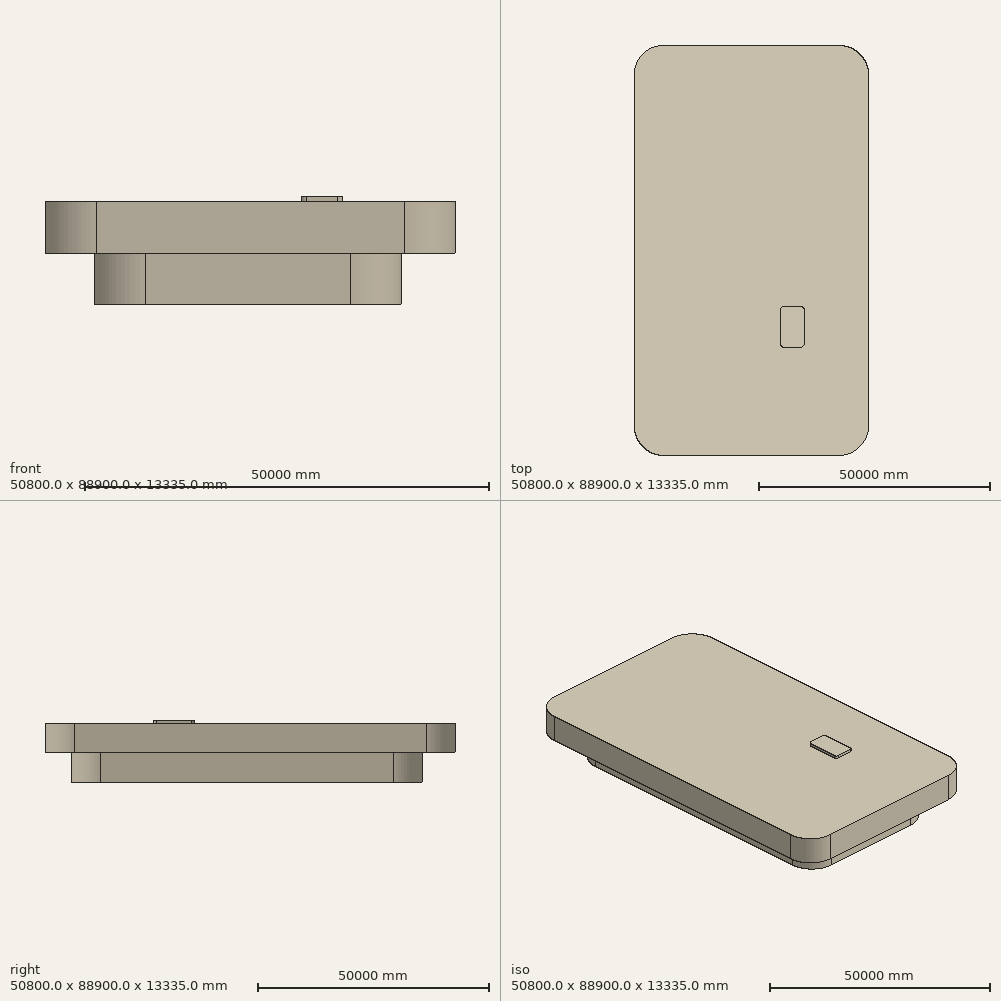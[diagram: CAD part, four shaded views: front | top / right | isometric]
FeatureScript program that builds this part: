
annotation { "Feature Type Name" : "Feature", "Feature Type Description" : "" }
export const myFeature = defineFeature(function(context is Context, id is Id, definition is map)
    precondition{}
    {
        {
            var Q0;
            Q0=qCreatedBy(makeId("Top.planeOp"),FACE);
            var sketch = newSketch(context, id + "F0", { "sketchPlane" : qUnion([Q0])});
            skLineSegment(sketch, "E0.bottom", {"start": v(591.8, -694.37) * mm, "end": v(1353.8, -694.37) * mm});
            skLineSegment(sketch, "E0.top", {"start": v(591.8, -186.37) * mm, "end": v(1353.8, -186.37) * mm});
            skLineSegment(sketch, "E0.left", {"start": v(528.3, -630.87) * mm, "end": v(528.3, -249.87) * mm});
            skLineSegment(sketch, "E0.right", {"start": v(1417.3, -630.87) * mm, "end": v(1417.3, -249.87) * mm});
            skPoint(sketch, "E1.visualSharp", {"position": v(1417.3, -186.37) * mm});
            skArc(sketch, "E1.filletArc", {"start": v(1417.3, -249.87) * mm, "mid": v(1398.7, -204.97) * mm, "end": v(1353.8, -186.37) * mm});
            skPoint(sketch, "E2.visualSharp", {"position": v(1417.3, -694.37) * mm});
            skArc(sketch, "E2.filletArc", {"start": v(1353.8, -694.37) * mm, "mid": v(1398.7, -675.78) * mm, "end": v(1417.3, -630.87) * mm});
            skPoint(sketch, "E3.visualSharp", {"position": v(528.3, -694.37) * mm});
            skArc(sketch, "E3.filletArc", {"start": v(528.3, -630.87) * mm, "mid": v(546.9, -675.78) * mm, "end": v(591.8, -694.37) * mm});
            skPoint(sketch, "E4.visualSharp", {"position": v(528.3, -186.37) * mm});
            skArc(sketch, "E4.filletArc", {"start": v(591.8, -186.37) * mm, "mid": v(546.9, -204.97) * mm, "end": v(528.3, -249.87) * mm});
            skSolve(sketch);
        }
        {
            var Q0;
            Q0 = qSketchRegion(id + "F0", true);
            extrude(context, id + "F1", {"entities" : qUnion([Q0]), "depth" : 6.35 * mm});
        }
        {
            var Q0;
            Q0=makeQuery(id+"F1.opExtrude","CAP_FACE",FACE,{"disambiguationData":[OSD([sQuery(id+"F0.wireOp",EDGE,"E0.bottom"),sQuery(id+"F0.wireOp",EDGE,"E0.top"),sQuery(id+"F0.wireOp",EDGE,"E0.left"),sQuery(id+"F0.wireOp",EDGE,"E0.right"),sQuery(id+"F0.wireOp",EDGE,"E1.filletArc"),sQuery(id+"F0.wireOp",EDGE,"E2.filletArc"),sQuery(id+"F0.wireOp",EDGE,"E3.filletArc"),sQuery(id+"F0.wireOp",EDGE,"E4.filletArc")])],"isStart":false});
            cPlane(context, id + "F2", {"entities" : qUnion([Q0]), "cplaneType" : CPlaneType.OFFSET, "offset" : 25.4 * mm, "width" : 152.4 * mm, "height" : 152.4 * mm});
        }
        {
            var Q0;
            Q0=qCreatedBy(id+"F2.planeOp",FACE);
            var sketch = newSketch(context, id + "F3", { "sketchPlane" : qUnion([Q0])});
            skLineSegment(sketch, "E5.bottom", {"start": v(591.8, -694.37) * mm, "end": v(1353.8, -694.37) * mm});
            skLineSegment(sketch, "E5.top", {"start": v(591.8, -186.37) * mm, "end": v(1353.8, -186.37) * mm});
            skLineSegment(sketch, "E5.left", {"start": v(528.3, -630.87) * mm, "end": v(528.3, -249.87) * mm});
            skLineSegment(sketch, "E5.right", {"start": v(1417.3, -630.87) * mm, "end": v(1417.3, -249.87) * mm});
            skPoint(sketch, "E6.visualSharp", {"position": v(1417.3, -186.37) * mm});
            skArc(sketch, "E6.filletArc", {"start": v(1417.3, -249.87) * mm, "mid": v(1398.7, -204.97) * mm, "end": v(1353.8, -186.37) * mm});
            skPoint(sketch, "E7.visualSharp", {"position": v(1417.3, -694.37) * mm});
            skArc(sketch, "E7.filletArc", {"start": v(1353.8, -694.37) * mm, "mid": v(1398.7, -675.78) * mm, "end": v(1417.3, -630.87) * mm});
            skPoint(sketch, "E8.visualSharp", {"position": v(528.3, -694.37) * mm});
            skArc(sketch, "E8.filletArc", {"start": v(528.3, -630.87) * mm, "mid": v(546.9, -675.78) * mm, "end": v(591.8, -694.37) * mm});
            skPoint(sketch, "E9.visualSharp", {"position": v(528.3, -186.37) * mm});
            skArc(sketch, "E9.filletArc", {"start": v(591.8, -186.37) * mm, "mid": v(546.9, -204.97) * mm, "end": v(528.3, -249.87) * mm});
            skSolve(sketch);
        }
        {
            var Q0;
            Q0=makeQuery(id+"F3.imprint","IMPRINT",FACE,{"disambiguationData":[TD([[makeQuery(id+"F3.imprint","IMPRINT",EDGE,{"derivedFrom":sQuery(id+"F3.wireOp",EDGE,"E5.bottom")}),1.0]])]});
            var Q1;
            Q1=sQuery(id+"F3.wireOp",EDGE,"E5.right");
            var Q2;
            Q2=sQuery(id+"F3.wireOp",EDGE,"E8.filletArc");
            var Q3;
            Q3=sQuery(id+"F3.wireOp",EDGE,"E6.filletArc");
            var Q4;
            Q4=sQuery(id+"F3.wireOp",EDGE,"E5.bottom");
            var Q5;
            Q5=sQuery(id+"F3.wireOp",EDGE,"E9.filletArc");
            var Q6;
            Q6=sQuery(id+"F3.wireOp",EDGE,"E7.filletArc");
            var Q7;
            Q7=sQuery(id+"F3.wireOp",EDGE,"E5.top");
            var Q8;
            Q8=sQuery(id+"F3.wireOp",EDGE,"E5.left");
            extrude(context, id + "F4", {"entities" : qUnion([Q0]), "surfaceEntities" : qUnion([Q1, Q2, Q3, Q4, Q5, Q6, Q7, Q8]), "depth" : 6.35 * mm});
        }
        {
            var Q0;
            Q0=qCreatedBy(id+"F2.planeOp",FACE);
            cPlane(context, id + "F5", {"entities" : qUnion([Q0]), "cplaneType" : CPlaneType.OFFSET, "offset" : 25.4 * mm, "width" : 152.4 * mm, "height" : 152.4 * mm});
        }
        {
            var Q0;
            Q0=qCreatedBy(id+"F5.planeOp",FACE);
            var sketch = newSketch(context, id + "F6", { "sketchPlane" : qUnion([Q0])});
            skLineSegment(sketch, "E10.bottom", {"start": v(591.8, -694.37) * mm, "end": v(1353.8, -694.37) * mm});
            skLineSegment(sketch, "E10.top", {"start": v(591.8, -186.37) * mm, "end": v(1353.8, -186.37) * mm});
            skLineSegment(sketch, "E10.left", {"start": v(528.3, -630.87) * mm, "end": v(528.3, -249.87) * mm});
            skLineSegment(sketch, "E10.right", {"start": v(1417.3, -630.87) * mm, "end": v(1417.3, -249.87) * mm});
            skPoint(sketch, "E11.visualSharp", {"position": v(1417.3, -186.37) * mm});
            skArc(sketch, "E11.filletArc", {"start": v(1417.3, -249.87) * mm, "mid": v(1398.7, -204.97) * mm, "end": v(1353.8, -186.37) * mm});
            skPoint(sketch, "E12.visualSharp", {"position": v(1417.3, -694.37) * mm});
            skArc(sketch, "E12.filletArc", {"start": v(1353.8, -694.37) * mm, "mid": v(1398.7, -675.78) * mm, "end": v(1417.3, -630.87) * mm});
            skPoint(sketch, "E13.visualSharp", {"position": v(528.3, -694.37) * mm});
            skArc(sketch, "E13.filletArc", {"start": v(528.3, -630.87) * mm, "mid": v(546.9, -675.78) * mm, "end": v(591.8, -694.37) * mm});
            skPoint(sketch, "E14.visualSharp", {"position": v(528.3, -186.37) * mm});
            skArc(sketch, "E14.filletArc", {"start": v(591.8, -186.37) * mm, "mid": v(546.9, -204.97) * mm, "end": v(528.3, -249.87) * mm});
            skSolve(sketch);
        }
        {
            var Q0;
            Q0 = qSketchRegion(id + "F6", true);
            var Q1;
            Q1=makeQuery(id+"F6.imprint","IMPRINT",FACE,{"disambiguationData":[TD([[makeQuery(id+"F6.imprint","IMPRINT",EDGE,{"derivedFrom":sQuery(id+"F6.wireOp",EDGE,"E10.bottom")}),1.0]])]});
            extrude(context, id + "F7", {"entities" : qUnion([Q0, Q1]), "depth" : 6.35 * mm});
        }
        {
            var Q0;
            Q0=qCreatedBy(makeId("Top.planeOp"),FACE);
            var sketch = newSketch(context, id + "F8", { "sketchPlane" : qUnion([Q0])});
            skLineSegment(sketch, "E15.bottom", {"start": v(-2759.22, -3519.53) * mm, "end": v(1050.78, -3519.53) * mm});
            skLineSegment(sketch, "E15.top", {"start": v(-2759.22, 5370.47) * mm, "end": v(1050.78, 5370.47) * mm});
            skLineSegment(sketch, "E15.left", {"start": v(-3394.22, -2884.53) * mm, "end": v(-3394.22, 4735.47) * mm});
            skLineSegment(sketch, "E15.right", {"start": v(1685.78, -2884.53) * mm, "end": v(1685.78, 4735.47) * mm});
            skPoint(sketch, "E16.visualSharp", {"position": v(1685.78, 5370.47) * mm});
            skArc(sketch, "E16.filletArc", {"start": v(1685.78, 4735.47) * mm, "mid": v(1499.8, 5184.48) * mm, "end": v(1050.78, 5370.47) * mm});
            skPoint(sketch, "E17.visualSharp", {"position": v(-3394.22, 5370.47) * mm});
            skArc(sketch, "E17.filletArc", {"start": v(-2759.22, 5370.47) * mm, "mid": v(-3208.23, 5184.48) * mm, "end": v(-3394.22, 4735.47) * mm});
            skPoint(sketch, "E18.visualSharp", {"position": v(-3394.22, -3519.53) * mm});
            skArc(sketch, "E18.filletArc", {"start": v(-3394.22, -2884.53) * mm, "mid": v(-3208.23, -3333.54) * mm, "end": v(-2759.22, -3519.53) * mm});
            skPoint(sketch, "E19.visualSharp", {"position": v(1685.78, -3519.53) * mm});
            skArc(sketch, "E19.filletArc", {"start": v(1050.78, -3519.53) * mm, "mid": v(1499.8, -3333.54) * mm, "end": v(1685.78, -2884.53) * mm});
            skSolve(sketch);
        }
        {
            var Q0;
            Q0=makeQuery(id+"F8.imprint","IMPRINT",FACE,{"disambiguationData":[TD([[makeQuery(id+"F8.imprint","IMPRINT",EDGE,{"derivedFrom":sQuery(id+"F8.wireOp",EDGE,"E15.bottom")}),1.0]])]});
            extrude(context, id + "F9", {"entities" : qUnion([Q0]), "depth" : 635 * mm});
        }
        {
            var Q0;
            Q0=makeQuery(id+"F9.opExtrude","CAP_FACE",FACE,{"disambiguationData":[OSD([sQuery(id+"F8.wireOp",EDGE,"E15.bottom"),sQuery(id+"F8.wireOp",EDGE,"E15.top"),sQuery(id+"F8.wireOp",EDGE,"E15.left"),sQuery(id+"F8.wireOp",EDGE,"E15.right"),sQuery(id+"F8.wireOp",EDGE,"E16.filletArc"),sQuery(id+"F8.wireOp",EDGE,"E17.filletArc"),sQuery(id+"F8.wireOp",EDGE,"E18.filletArc"),sQuery(id+"F8.wireOp",EDGE,"E19.filletArc")])],"isStart":true});
            var sketch = newSketch(context, id + "F10", { "sketchPlane" : qUnion([Q0])});
            skLineSegment(sketch, "E20.bottom", {"start": v(-28802.53, 26934.52) * mm, "end": v(9297.47, 26934.52) * mm});
            skLineSegment(sketch, "E20.top", {"start": v(-28802.53, -61965.48) * mm, "end": v(9297.47, -61965.48) * mm});
            skLineSegment(sketch, "E20.left", {"start": v(-35152.53, 20584.52) * mm, "end": v(-35152.53, -55615.48) * mm});
            skLineSegment(sketch, "E20.right", {"start": v(15647.47, 20584.52) * mm, "end": v(15647.47, -55615.48) * mm});
            skPoint(sketch, "E21.visualSharp", {"position": v(15647.47, -61965.48) * mm});
            skArc(sketch, "E21.filletArc", {"start": v(9297.47, -61965.48) * mm, "mid": v(13787.6, -60105.6) * mm, "end": v(15647.47, -55615.48) * mm});
            skPoint(sketch, "E22.visualSharp", {"position": v(-35152.53, -61965.48) * mm});
            skArc(sketch, "E22.filletArc", {"start": v(-35152.53, -55615.48) * mm, "mid": v(-33292.66, -60105.6) * mm, "end": v(-28802.53, -61965.48) * mm});
            skPoint(sketch, "E23.visualSharp", {"position": v(-35152.53, 26934.52) * mm});
            skArc(sketch, "E23.filletArc", {"start": v(-28802.53, 26934.52) * mm, "mid": v(-33292.66, 25074.65) * mm, "end": v(-35152.53, 20584.52) * mm});
            skPoint(sketch, "E24.visualSharp", {"position": v(15647.47, 26934.52) * mm});
            skArc(sketch, "E24.filletArc", {"start": v(15647.47, 20584.52) * mm, "mid": v(13787.6, 25074.65) * mm, "end": v(9297.47, 26934.52) * mm});
            skSolve(sketch);
        }
        {
            var Q0;
            Q0 = qSketchRegion(id + "F10", true);
            extrude(context, id + "F11", {"entities" : qUnion([Q0]), "depth" : 6350 * mm});
        }
        {
            var Q0;
            Q0=makeQuery(id+"F11.opExtrude","CAP_FACE",FACE,{"disambiguationData":[OSD([sQuery(id+"F10.wireOp",EDGE,"E20.bottom"),sQuery(id+"F10.wireOp",EDGE,"E20.top"),sQuery(id+"F10.wireOp",EDGE,"E20.left"),sQuery(id+"F10.wireOp",EDGE,"E20.right"),sQuery(id+"F10.wireOp",EDGE,"E21.filletArc"),sQuery(id+"F10.wireOp",EDGE,"E22.filletArc"),sQuery(id+"F10.wireOp",EDGE,"E23.filletArc"),sQuery(id+"F10.wireOp",EDGE,"E24.filletArc")])],"isStart":false});
            var sketch = newSketch(context, id + "F12", { "sketchPlane" : qUnion([Q0])});
            skLineSegment(sketch, "E25.bottom", {"start": v(-22766.31, 21391.5) * mm, "end": v(2633.69, 21391.5) * mm});
            skLineSegment(sketch, "E25.top", {"start": v(-22766.31, -54808.5) * mm, "end": v(2633.69, -54808.5) * mm});
            skLineSegment(sketch, "E25.left", {"start": v(-29116.31, 15041.5) * mm, "end": v(-29116.31, -48458.5) * mm});
            skLineSegment(sketch, "E25.right", {"start": v(8983.69, 15041.5) * mm, "end": v(8983.69, -48458.5) * mm});
            skPoint(sketch, "E26.visualSharp", {"position": v(8983.69, -54808.5) * mm});
            skArc(sketch, "E26.filletArc", {"start": v(2633.69, -54808.5) * mm, "mid": v(7123.82, -52948.62) * mm, "end": v(8983.69, -48458.5) * mm});
            skPoint(sketch, "E27.visualSharp", {"position": v(-29116.31, -54808.5) * mm});
            skArc(sketch, "E27.filletArc", {"start": v(-29116.31, -48458.5) * mm, "mid": v(-27256.44, -52948.62) * mm, "end": v(-22766.31, -54808.5) * mm});
            skPoint(sketch, "E28.visualSharp", {"position": v(-29116.31, 21391.5) * mm});
            skArc(sketch, "E28.filletArc", {"start": v(-22766.31, 21391.5) * mm, "mid": v(-27256.44, 19531.63) * mm, "end": v(-29116.31, 15041.5) * mm});
            skPoint(sketch, "E29.visualSharp", {"position": v(8983.69, 21391.5) * mm});
            skArc(sketch, "E29.filletArc", {"start": v(8983.69, 15041.5) * mm, "mid": v(7123.82, 19531.63) * mm, "end": v(2633.69, 21391.5) * mm});
            skSolve(sketch);
        }
        {
            var Q0;
            Q0 = qSketchRegion(id + "F12", true);
            extrude(context, id + "F13", {"entities" : qUnion([Q0]), "depth" : 6350 * mm});
        }
    });
